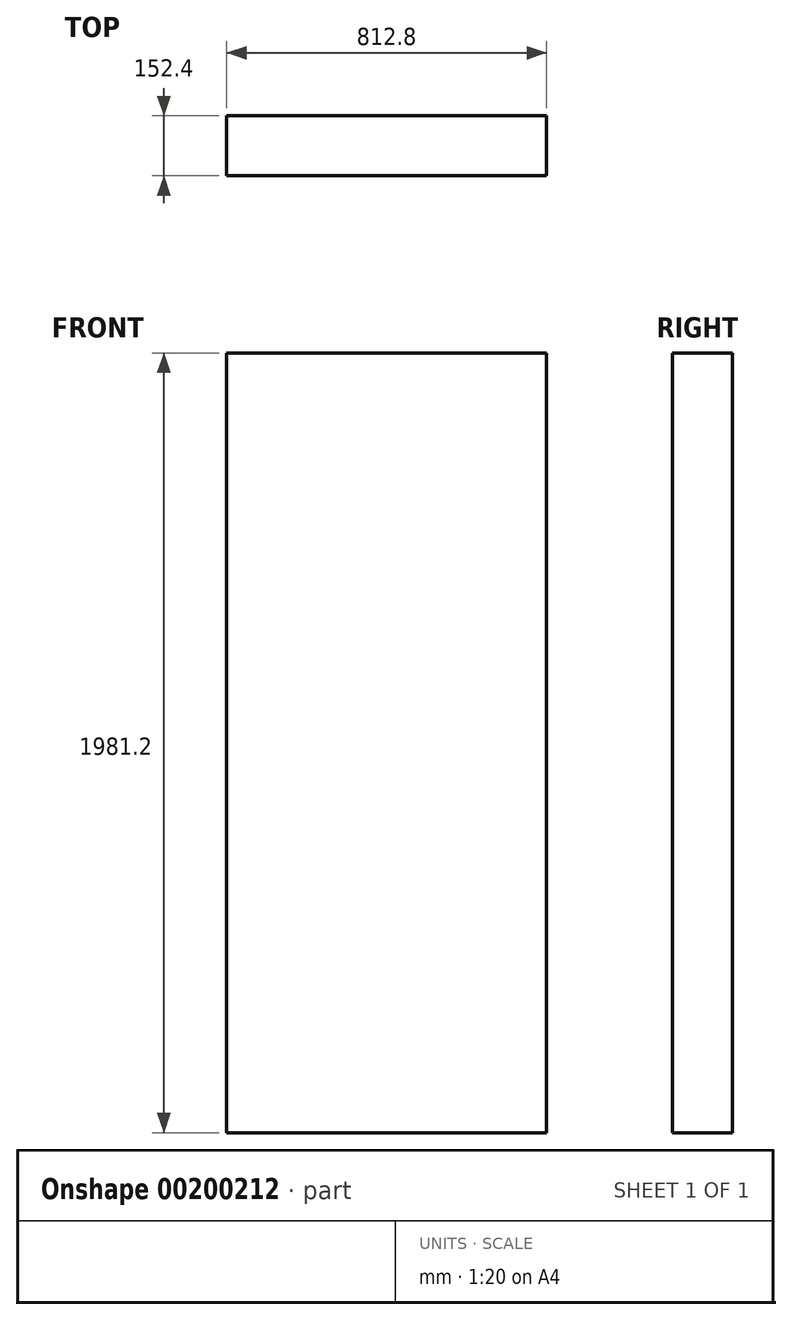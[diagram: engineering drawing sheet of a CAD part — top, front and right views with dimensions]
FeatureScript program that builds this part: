
annotation { "Feature Type Name" : "Feature", "Feature Type Description" : "" }
export const myFeature = defineFeature(function(context is Context, id is Id, definition is map)
    precondition{}
    {
        {
            var Q0;
            Q0=qCreatedBy(makeId("Front.planeOp"),FACE);
            var sketch = newSketch(context, id + "F0", { "sketchPlane" : qUnion([Q0])});
            skLineSegment(sketch, "E0.bottom", {"start": v(-1050.7, 941.05) * mm, "end": v(-237.9, 941.05) * mm});
            skLineSegment(sketch, "E0.top", {"start": v(-1050.7, -1040.15) * mm, "end": v(-237.9, -1040.15) * mm});
            skLineSegment(sketch, "E0.left", {"start": v(-1050.7, 941.05) * mm, "end": v(-1050.7, -1040.15) * mm});
            skLineSegment(sketch, "E0.right", {"start": v(-237.9, 941.05) * mm, "end": v(-237.9, -1040.15) * mm});
            skSolve(sketch);
        }
        {
            var Q0;
            Q0 = qSketchRegion(id + "F0", true);
            extrude(context, id + "F1", {"entities" : qUnion([Q0]), "depth" : 152.4 * mm});
        }
    });
